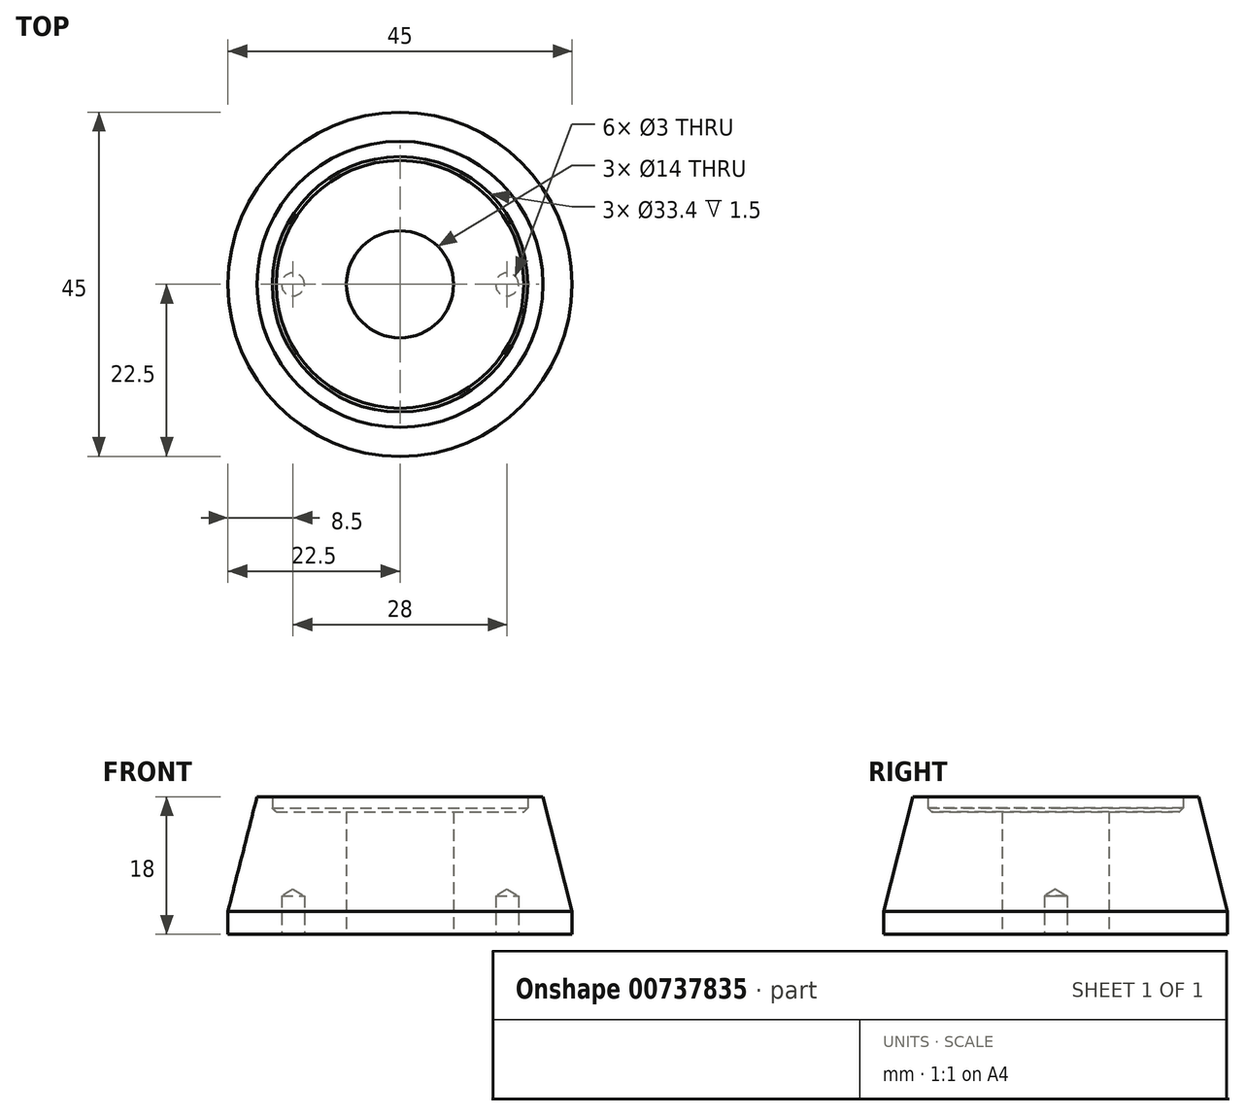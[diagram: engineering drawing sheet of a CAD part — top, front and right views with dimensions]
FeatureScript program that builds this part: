
annotation { "Feature Type Name" : "Feature", "Feature Type Description" : "" }
export const myFeature = defineFeature(function(context is Context, id is Id, definition is map)
    precondition{}
    {
        {
            var Q0;
            Q0=qCreatedBy(makeId("Front.planeOp"),FACE);
            var sketch = newSketch(context, id + "F0", { "sketchPlane" : qUnion([Q0])});
            skLineSegment(sketch, "E0", {"start": v(0, 20.62) * mm, "end": v(-22.5, 20.62) * mm});
            skLineSegment(sketch, "E1", {"start": v(0, 20.62) * mm, "end": v(0, 36.62) * mm});
            skLineSegment(sketch, "E2", {"start": v(0, 36.62) * mm, "end": v(-16.2, 36.62) * mm});
            skLineSegment(sketch, "E3", {"start": v(-7, 36.62) * mm, "end": v(-7, 20.62) * mm});
            skLineSegment(sketch, "E4", {"start": v(-22.5, 20.62) * mm, "end": v(-22.5, 23.62) * mm});
            skLineSegment(sketch, "E5", {"start": v(-22.5, 23.62) * mm, "end": v(-18.7, 38.62) * mm});
            skLineSegment(sketch, "E6", {"start": v(-18.7, 38.62) * mm, "end": v(-16.7, 38.62) * mm});
            skLineSegment(sketch, "E7", {"start": v(-16.7, 38.62) * mm, "end": v(-16.7, 37.12) * mm});
            skLineSegment(sketch, "E8", {"start": v(-16.7, 37.12) * mm, "end": v(-16.2, 36.62) * mm});
            skSolve(sketch);
        }
        {
            var Q0;
            {var subQ0=sQuery(id+"F0.wireOp",EDGE,"E3");Q0=makeQuery(id+"F0.imprint","IMPRINT",FACE,{"disambiguationData":[TD([[makeQuery(id+"F0.imprint","IMPRINT",EDGE,{"derivedFrom":subQ0}),-1.0]])]});}
            var Q1;
            Q1=sQuery(id+"F0.wireOp",EDGE,"E1");
            revolve(context, id + "F1", {"entities" : qUnion([Q0]), "axis" : qUnion([Q1]), "revolveType" : RevolveType.FULL});
        }
        {
            var Q0;
            Q0=makeQuery(id+"F1.opRevolve","SWEPT_FACE",FACE,{"disambiguationData":[OSD([sQuery(id+"F0.wireOp",EDGE,"E0")])]});
            var sketch = newSketch(context, id + "F2", { "sketchPlane" : qUnion([Q0])});
            skPoint(sketch, "E9", {"position": v(-14, 0) * mm});
            skPoint(sketch, "E10.1.0", {"position": v(14, 0) * mm});
            skPoint(sketch, "E10.center", {"position": v(0, 0) * mm});
            skSolve(sketch);
        }
        {
            var Q0;
            Q0=sQuery(id+"F2.wireOp",VERTEX,"E9");
            var Q1;
            Q1=sQuery(id+"F2.wireOp",VERTEX,"E10.1.0");
            var Q2;
            Q2=makeQuery(id+"F1.opRevolve","SWEPT_BODY",BODY,{"disambiguationData":[OSD([sQuery(id+"F0.wireOp",EDGE,"E0"),sQuery(id+"F0.wireOp",EDGE,"E2"),sQuery(id+"F0.wireOp",EDGE,"I1IZs9et-yzp2-pkoH-Uqyj-Zst5VyObDKE9"),sQuery(id+"F0.wireOp",EDGE,"TEGZxwhD-VCsi-AP2g-Tj0f-wSHnz4qmJ26e"),sQuery(id+"F0.wireOp",EDGE,"TgjRPXJ9-tEQl-qVCL-aCPt-cUJG5a0YcU9j"),sQuery(id+"F0.wireOp",EDGE,"E3")])]});
            hole(context, id + "F3", {"style" : HoleStyle.SIMPLE, "endStyle" : HoleEndStyle.BLIND, "holeDiameter" : 3 * mm, "holeDepth" : 5 * mm, "isTappedThrough" : true, "tappedDepth" : 12 * mm, "tapClearance" : 3, "locations" : qUnion([Q0, Q1]), "scope" : qUnion([Q2]), "majorDiameter" : 5 * mm});
        }
    });
